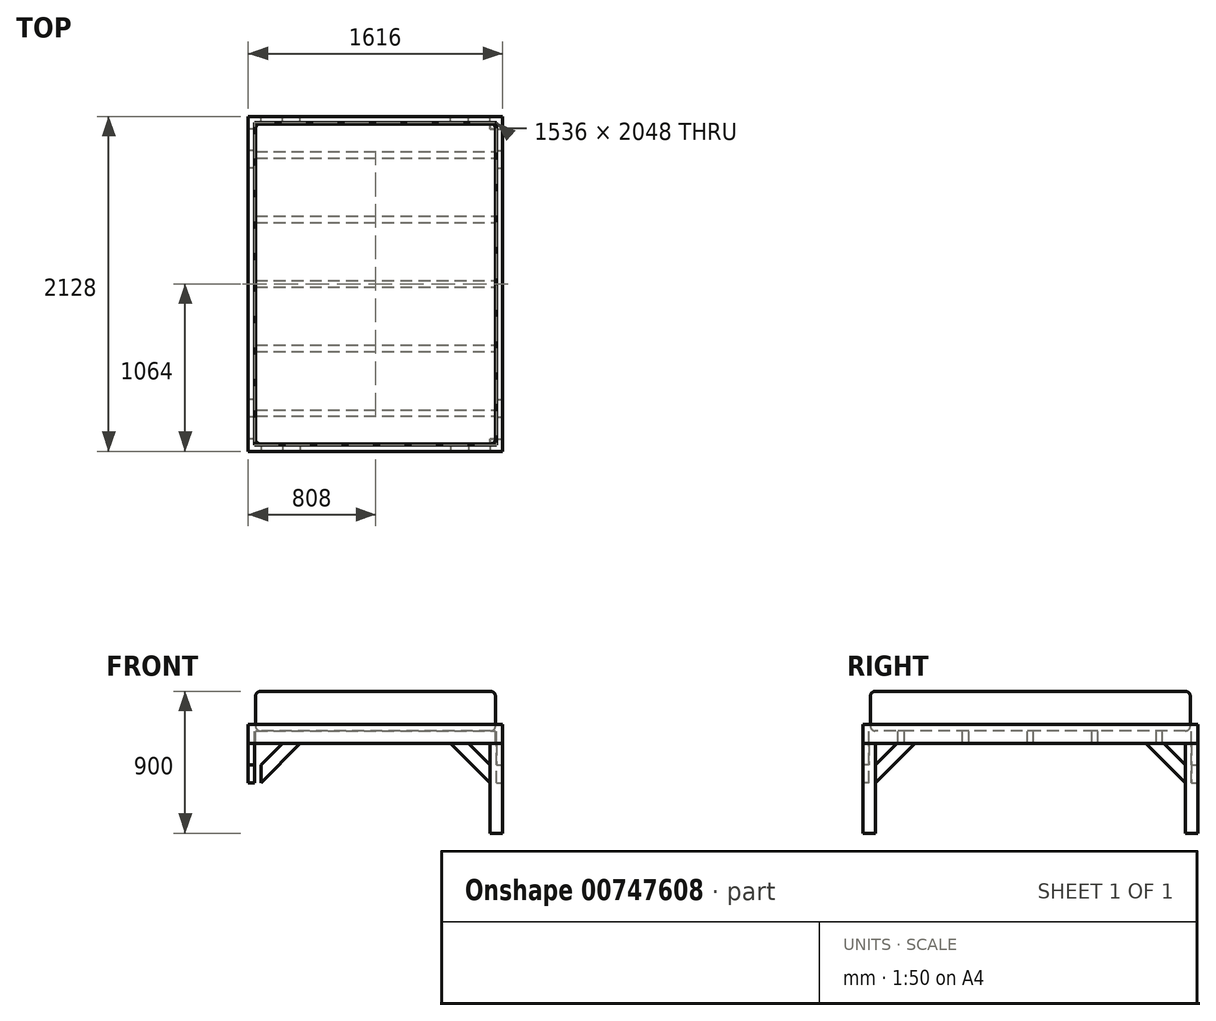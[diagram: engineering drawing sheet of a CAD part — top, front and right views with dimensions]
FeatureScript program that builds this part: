
annotation { "Feature Type Name" : "Feature", "Feature Type Description" : "" }
export const myFeature = defineFeature(function(context is Context, id is Id, definition is map)
    precondition{}
    {
        {
            assignVariable(context, id + "F0", {"name" : "profile", "anyValue" : 40 * mm});
        }
        {
            var Q0;
            Q0=qCreatedBy(makeId("Top.planeOp"),FACE);
            var sketch = newSketch(context, id + "F1", { "sketchPlane" : qUnion([Q0])});
            skLineSegment(sketch, "E0.bottom", {"start": v(762, 1016) * mm, "end": v(-762, 1016) * mm});
            skLineSegment(sketch, "E0.top", {"start": v(762, -1016) * mm, "end": v(-762, -1016) * mm});
            skLineSegment(sketch, "E0.left", {"start": v(762, 1016) * mm, "end": v(762, -1016) * mm});
            skLineSegment(sketch, "E0.right", {"start": v(-762, 1016) * mm, "end": v(-762, -1016) * mm});
            skPoint(sketch, "E0.middle", {"position": v(0, 0) * mm});
            skSolve(sketch);
        }
        {
            var Q0;
            Q0=makeQuery(id+"F1.imprint","IMPRINT",FACE,{"disambiguationData":[TD([[makeQuery(id+"F1.imprint","IMPRINT",EDGE,{"derivedFrom":sQuery(id+"F1.wireOp",EDGE,"E0.bottom")}),1.0]])]});
            extrude(context, id + "F2", {"entities" : qUnion([Q0]), "depth" : 250 * mm, "offsetDistance" : 25 * mm});
        }
        {
            var Q0;
            Q0=makeQuery(id+"F2.opExtrude","CAP_EDGE",EDGE,{"disambiguationData":[OSD([sQuery(id+"F1.wireOp",EDGE,"E0.right")])],"isStart":false});
            var Q1;
            Q1=makeQuery(id+"F2.opExtrude","CAP_EDGE",EDGE,{"disambiguationData":[OSD([sQuery(id+"F1.wireOp",EDGE,"E0.bottom")])],"isStart":false});
            var Q2;
            Q2=makeQuery(id+"F2.opExtrude","CAP_EDGE",EDGE,{"disambiguationData":[OSD([sQuery(id+"F1.wireOp",EDGE,"E0.left")])],"isStart":false});
            var Q3;
            Q3=makeQuery(id+"F2.opExtrude","CAP_EDGE",EDGE,{"disambiguationData":[OSD([sQuery(id+"F1.wireOp",EDGE,"E0.top")])],"isStart":false});
            var Q4;
            Q4=makeQuery(id+"F2.opExtrude","SWEPT_EDGE",EDGE,{"disambiguationData":[OSD([sQuery(id+"F1.wireOp",EDGE,"E0.top"),sQuery(id+"F1.wireOp",EDGE,"E0.right")])]});
            var Q5;
            Q5=makeQuery(id+"F2.opExtrude","SWEPT_EDGE",EDGE,{"disambiguationData":[OSD([sQuery(id+"F1.wireOp",EDGE,"E0.bottom"),sQuery(id+"F1.wireOp",EDGE,"E0.right")])]});
            var Q6;
            Q6=makeQuery(id+"F2.opExtrude","SWEPT_EDGE",EDGE,{"disambiguationData":[OSD([sQuery(id+"F1.wireOp",EDGE,"E0.top"),sQuery(id+"F1.wireOp",EDGE,"E0.left")])]});
            var Q7;
            Q7=makeQuery(id+"F2.opExtrude","CAP_EDGE",EDGE,{"disambiguationData":[OSD([sQuery(id+"F1.wireOp",EDGE,"E0.top")])],"isStart":true});
            var Q8;
            Q8=makeQuery(id+"F2.opExtrude","CAP_EDGE",EDGE,{"disambiguationData":[OSD([sQuery(id+"F1.wireOp",EDGE,"E0.right")])],"isStart":true});
            var Q9;
            Q9=makeQuery(id+"F2.opExtrude","SWEPT_EDGE",EDGE,{"disambiguationData":[OSD([sQuery(id+"F1.wireOp",EDGE,"E0.bottom"),sQuery(id+"F1.wireOp",EDGE,"E0.left")])]});
            var Q10;
            Q10=makeQuery(id+"F2.opExtrude","CAP_EDGE",EDGE,{"disambiguationData":[OSD([sQuery(id+"F1.wireOp",EDGE,"E0.left")])],"isStart":true});
            var Q11;
            Q11=makeQuery(id+"F2.opExtrude","CAP_EDGE",EDGE,{"disambiguationData":[OSD([sQuery(id+"F1.wireOp",EDGE,"E0.bottom")])],"isStart":true});
            fillet(context, id + "F3", {"entities" : qUnion([Q0, Q1, Q2, Q3, Q4, Q5, Q6, Q7, Q8, Q9, Q10, Q11]), "radius" : 30 * mm, "tangentPropagation" : true, "allowEdgeOverflow" : false});
        }
        {
            var Q0;
            Q0=makeQuery(id+"F1.imprint","IMPRINT",FACE,{"disambiguationData":[TD([[makeQuery(id+"F1.imprint","IMPRINT",EDGE,{"derivedFrom":sQuery(id+"F1.wireOp",EDGE,"E0.bottom")}),1.0]])]});
            var sketch = newSketch(context, id + "F4", { "sketchPlane" : qUnion([Q0])});
            skLineSegment(sketch, "E1.bottom", {"start": v(768, 1024) * mm, "end": v(-768, 1024) * mm});
            skLineSegment(sketch, "E1.top", {"start": v(768, -1024) * mm, "end": v(-768, -1024) * mm});
            skLineSegment(sketch, "E1.left", {"start": v(768, 1024) * mm, "end": v(768, -1024) * mm});
            skLineSegment(sketch, "E1.right", {"start": v(-768, 1024) * mm, "end": v(-768, -1024) * mm});
            skPoint(sketch, "E1.middle", {"position": v(0, 0) * mm});
            skLineSegment(sketch, "E2.bottom", {"start": v(808, 1064) * mm, "end": v(-808, 1064) * mm});
            skLineSegment(sketch, "E2.top", {"start": v(808, -1064) * mm, "end": v(-808, -1064) * mm});
            skLineSegment(sketch, "E2.left", {"start": v(808, 1064) * mm, "end": v(808, -1064) * mm});
            skLineSegment(sketch, "E2.right", {"start": v(-808, 1064) * mm, "end": v(-808, -1064) * mm});
            skLineSegment(sketch, "E3", {"start": v(-768, 1024) * mm, "end": v(-768, 1064) * mm});
            skLineSegment(sketch, "E4", {"start": v(768, 1024) * mm, "end": v(768, 1064) * mm});
            skLineSegment(sketch, "E5", {"start": v(768, -1024) * mm, "end": v(768, -1064) * mm});
            skLineSegment(sketch, "E6", {"start": v(-768, -1024) * mm, "end": v(-768, -1064) * mm});
            skLineSegment(sketch, "E7.bottom", {"start": v(-768, 840) * mm, "end": v(768, 840) * mm});
            skLineSegment(sketch, "E7.top", {"start": v(-768, 800) * mm, "end": v(768, 800) * mm});
            skLineSegment(sketch, "E7.left", {"start": v(-768, 840) * mm, "end": v(-768, 800) * mm});
            skLineSegment(sketch, "E7.right", {"start": v(768, 840) * mm, "end": v(768, 800) * mm});
            skLineSegment(sketch, "E8.bottom", {"start": v(-768, 20) * mm, "end": v(768, 20) * mm});
            skLineSegment(sketch, "E8.top", {"start": v(-768, -20) * mm, "end": v(768, -20) * mm});
            skLineSegment(sketch, "E8.left", {"start": v(-768, 20) * mm, "end": v(-768, -20) * mm});
            skLineSegment(sketch, "E8.right", {"start": v(768, 20) * mm, "end": v(768, -20) * mm});
            skLineSegment(sketch, "E9.bottom", {"start": v(-768, -800) * mm, "end": v(768, -800) * mm});
            skLineSegment(sketch, "E9.top", {"start": v(-768, -840) * mm, "end": v(768, -840) * mm});
            skLineSegment(sketch, "E9.left", {"start": v(-768, -800) * mm, "end": v(-768, -840) * mm});
            skLineSegment(sketch, "E9.right", {"start": v(768, -800) * mm, "end": v(768, -840) * mm});
            skLineSegment(sketch, "E10.bottom", {"start": v(-768, 430) * mm, "end": v(768, 430) * mm});
            skLineSegment(sketch, "E10.top", {"start": v(-768, 390) * mm, "end": v(768, 390) * mm});
            skLineSegment(sketch, "E10.left", {"start": v(-768, 430) * mm, "end": v(-768, 390) * mm});
            skLineSegment(sketch, "E10.right", {"start": v(768, 430) * mm, "end": v(768, 390) * mm});
            skLineSegment(sketch, "E11.bottom", {"start": v(-768, -390) * mm, "end": v(768, -390) * mm});
            skLineSegment(sketch, "E11.top", {"start": v(-768, -430) * mm, "end": v(768, -430) * mm});
            skLineSegment(sketch, "E11.left", {"start": v(-768, -390) * mm, "end": v(-768, -430) * mm});
            skLineSegment(sketch, "E11.right", {"start": v(768, -390) * mm, "end": v(768, -430) * mm});
            skLineSegment(sketch, "E12", {"start": v(442.8, 800) * mm, "end": v(442.8, 430) * mm, "construction": true});
            skLineSegment(sketch, "E13", {"start": v(447.42, 390) * mm, "end": v(447.42, 20) * mm, "construction": true});
            skLineSegment(sketch, "E14", {"start": v(422, -20) * mm, "end": v(422, -390) * mm, "construction": true});
            skLineSegment(sketch, "E15", {"start": v(465.9, -430) * mm, "end": v(465.9, -800) * mm, "construction": true});
            skLineSegment(sketch, "E16", {"start": v(442.8, 615) * mm, "end": v(0, 615) * mm, "construction": true});
            skLineSegment(sketch, "E17", {"start": v(0, 615) * mm, "end": v(0, 800) * mm, "construction": true});
            skLineSegment(sketch, "E18", {"start": v(321.78, -840) * mm, "end": v(321.78, -1024) * mm, "construction": true});
            skLineSegment(sketch, "E19", {"start": v(177.4, 840) * mm, "end": v(177.4, 1024) * mm, "construction": true});
            skSolve(sketch);
        }
        {
            var Q0;
            {var subQ0=sQuery(id+"F4.wireOp",EDGE,"E2.right");Q0=makeQuery(id+"F4.imprint","IMPRINT",FACE,{"disambiguationData":[TD([[makeQuery(id+"F4.imprint","IMPRINT",EDGE,{"derivedFrom":subQ0}),1.0]])]});}
            var Q1;
            {var subQ1=sQuery(id+"F4.wireOp",EDGE,"E2.left");Q1=makeQuery(id+"F4.imprint","IMPRINT",FACE,{"disambiguationData":[TD([[makeQuery(id+"F4.imprint","IMPRINT",EDGE,{"derivedFrom":subQ1}),-1.0]])]});}
            extrude(context, id + "F5", {"entities" : qUnion([Q0, Q1]), "oppositeDirection" : true, "depth" : 2 * getVariable(context, 'profile'), "offsetDistance" : 25 * mm});
        }
        {
            var Q0;
            Q0=makeQuery(id+"F4.imprint","IMPRINT",FACE,{"disambiguationData":[TD([[makeQuery(id+"F4.imprint","IMPRINT",EDGE,{"derivedFrom":sQuery(id+"F4.wireOp",EDGE,"E1.bottom")}),-1.0]])]});
            var Q1;
            {var subQ0=sQuery(id+"F4.wireOp",EDGE,"E7.bottom");var subQ1=makeQuery(id+"F1.imprint","IMPRINT",EDGE,{"derivedFrom":sQuery(id+"F1.wireOp",EDGE,"E0.right")});var subQ2=makeQuery(id+"F4.imprint","INTERSECT",VERTEX,{"derivedFrom":[subQ1,subQ0]});Q1=makeQuery(id+"F4.imprint","IMPRINT",FACE,{"disambiguationData":[TD([[makeQuery(id+"F4.imprint","IMPRINT",EDGE,{"disambiguationData":[TD([[subQ2,-1.0]])],"derivedFrom":subQ0}),-1.0]])]});}
            var Q2;
            {var subQ0=sQuery(id+"F4.wireOp",EDGE,"E10.bottom");var subQ1=makeQuery(id+"F1.imprint","IMPRINT",EDGE,{"derivedFrom":sQuery(id+"F1.wireOp",EDGE,"E0.right")});var subQ2=makeQuery(id+"F4.imprint","INTERSECT",VERTEX,{"derivedFrom":[subQ1,subQ0]});Q2=makeQuery(id+"F4.imprint","IMPRINT",FACE,{"disambiguationData":[TD([[makeQuery(id+"F4.imprint","IMPRINT",EDGE,{"disambiguationData":[TD([[subQ2,-1.0]])],"derivedFrom":subQ0}),-1.0]])]});}
            var Q3;
            {var subQ0=sQuery(id+"F4.wireOp",EDGE,"E8.bottom");var subQ1=makeQuery(id+"F1.imprint","IMPRINT",EDGE,{"derivedFrom":sQuery(id+"F1.wireOp",EDGE,"E0.right")});var subQ2=makeQuery(id+"F4.imprint","INTERSECT",VERTEX,{"derivedFrom":[subQ1,subQ0]});Q3=makeQuery(id+"F4.imprint","IMPRINT",FACE,{"disambiguationData":[TD([[makeQuery(id+"F4.imprint","IMPRINT",EDGE,{"disambiguationData":[TD([[subQ2,-1.0]])],"derivedFrom":subQ0}),-1.0]])]});}
            var Q4;
            {var subQ0=sQuery(id+"F4.wireOp",EDGE,"E11.bottom");var subQ1=makeQuery(id+"F1.imprint","IMPRINT",EDGE,{"derivedFrom":sQuery(id+"F1.wireOp",EDGE,"E0.right")});var subQ2=makeQuery(id+"F4.imprint","INTERSECT",VERTEX,{"derivedFrom":[subQ1,subQ0]});Q4=makeQuery(id+"F4.imprint","IMPRINT",FACE,{"disambiguationData":[TD([[makeQuery(id+"F4.imprint","IMPRINT",EDGE,{"disambiguationData":[TD([[subQ2,-1.0]])],"derivedFrom":subQ0}),-1.0]])]});}
            var Q5;
            {var subQ0=sQuery(id+"F4.wireOp",EDGE,"E9.bottom");var subQ1=makeQuery(id+"F1.imprint","IMPRINT",EDGE,{"derivedFrom":sQuery(id+"F1.wireOp",EDGE,"E0.right")});var subQ2=makeQuery(id+"F4.imprint","INTERSECT",VERTEX,{"derivedFrom":[subQ1,subQ0]});Q5=makeQuery(id+"F4.imprint","IMPRINT",FACE,{"disambiguationData":[TD([[makeQuery(id+"F4.imprint","IMPRINT",EDGE,{"disambiguationData":[TD([[subQ2,-1.0]])],"derivedFrom":subQ0}),-1.0]])]});}
            var Q6;
            Q6=makeQuery(id+"F4.imprint","IMPRINT",FACE,{"disambiguationData":[TD([[makeQuery(id+"F4.imprint","IMPRINT",EDGE,{"derivedFrom":sQuery(id+"F4.wireOp",EDGE,"E1.top")}),1.0]])]});
            extrude(context, id + "F6", {"entities" : qUnion([Q0, Q1, Q2, Q3, Q4, Q5, Q6]), "oppositeDirection" : true, "depth" : 2 * getVariable(context, 'profile'), "offsetDistance" : 25 * mm});
        }
        {
            var Q0;
            {var subQ1=sQuery(id+"F4.wireOp",EDGE,"E2.left");Q0=makeQuery(id+"F4.imprint","IMPRINT",FACE,{"disambiguationData":[TD([[makeQuery(id+"F4.imprint","IMPRINT",EDGE,{"derivedFrom":subQ1}),-1.0]])]});}
            extrude(context, id + "F7", {"entities" : qUnion([Q0]), "operationType" : NewBodyOperationType.ADD, "depth" : getVariable(context, 'profile'), "offsetDistance" : 25 * mm});
        }
        {
            var Q0;
            Q0=makeQuery(id+"F4.imprint","IMPRINT",FACE,{"disambiguationData":[TD([[makeQuery(id+"F4.imprint","IMPRINT",EDGE,{"derivedFrom":sQuery(id+"F4.wireOp",EDGE,"E1.bottom")}),-1.0]])]});
            extrude(context, id + "F8", {"entities" : qUnion([Q0]), "operationType" : NewBodyOperationType.ADD, "depth" : getVariable(context, 'profile'), "offsetDistance" : 25 * mm});
        }
        {
            var Q0;
            {var subQ0=sQuery(id+"F4.wireOp",EDGE,"E2.right");Q0=makeQuery(id+"F4.imprint","IMPRINT",FACE,{"disambiguationData":[TD([[makeQuery(id+"F4.imprint","IMPRINT",EDGE,{"derivedFrom":subQ0}),1.0]])]});}
            extrude(context, id + "F9", {"entities" : qUnion([Q0]), "operationType" : NewBodyOperationType.ADD, "depth" : getVariable(context, 'profile'), "offsetDistance" : 25 * mm});
        }
        {
            var Q0;
            Q0=makeQuery(id+"F4.imprint","IMPRINT",FACE,{"disambiguationData":[TD([[makeQuery(id+"F4.imprint","IMPRINT",EDGE,{"derivedFrom":sQuery(id+"F4.wireOp",EDGE,"E1.top")}),1.0]])]});
            extrude(context, id + "F10", {"entities" : qUnion([Q0]), "operationType" : NewBodyOperationType.ADD, "depth" : getVariable(context, 'profile'), "offsetDistance" : 25 * mm});
        }
        {
            var Q0;
            Q0=makeQuery(id+"F5.opExtrude","CAP_FACE",FACE,{"disambiguationData":[OSD([sQuery(id+"F4.wireOp",EDGE,"E1.left"),sQuery(id+"F4.wireOp",EDGE,"E2.bottom"),sQuery(id+"F4.wireOp",EDGE,"E2.top"),sQuery(id+"F4.wireOp",EDGE,"E2.left"),sQuery(id+"F4.wireOp",EDGE,"E4"),sQuery(id+"F4.wireOp",EDGE,"E5"),sQuery(id+"F4.wireOp",EDGE,"E7.right"),sQuery(id+"F4.wireOp",EDGE,"E8.right"),sQuery(id+"F4.wireOp",EDGE,"E9.right"),sQuery(id+"F4.wireOp",EDGE,"E10.right"),sQuery(id+"F4.wireOp",EDGE,"E11.right")])],"isStart":false});
            var sketch = newSketch(context, id + "F11", { "sketchPlane" : qUnion([Q0])});
            skPoint(sketch, "E20.0", {"position": v(808, 1064) * mm});
            skPoint(sketch, "E21.0", {"position": v(808, -1064) * mm});
            skPoint(sketch, "E22.0", {"position": v(-808, -1064) * mm});
            skPoint(sketch, "E23.0", {"position": v(-808, 1064) * mm});
            skLineSegment(sketch, "E24.bottom", {"start": v(-808, 1064) * mm, "end": v(-728, 1064) * mm});
            skLineSegment(sketch, "E24.top", {"start": v(-808, 984) * mm, "end": v(-728, 984) * mm});
            skLineSegment(sketch, "E24.left", {"start": v(-808, 1064) * mm, "end": v(-808, 984) * mm});
            skLineSegment(sketch, "E24.right", {"start": v(-728, 1064) * mm, "end": v(-728, 984) * mm});
            skLineSegment(sketch, "E25.bottom", {"start": v(808, 1064) * mm, "end": v(728, 1064) * mm});
            skLineSegment(sketch, "E25.top", {"start": v(808, 984) * mm, "end": v(728, 984) * mm});
            skLineSegment(sketch, "E25.left", {"start": v(808, 1064) * mm, "end": v(808, 984) * mm});
            skLineSegment(sketch, "E25.right", {"start": v(728, 1064) * mm, "end": v(728, 984) * mm});
            skLineSegment(sketch, "E26.bottom", {"start": v(808, -1064) * mm, "end": v(728, -1064) * mm});
            skLineSegment(sketch, "E26.top", {"start": v(808, -984) * mm, "end": v(728, -984) * mm});
            skLineSegment(sketch, "E26.left", {"start": v(808, -1064) * mm, "end": v(808, -984) * mm});
            skLineSegment(sketch, "E26.right", {"start": v(728, -1064) * mm, "end": v(728, -984) * mm});
            skLineSegment(sketch, "E27.bottom", {"start": v(-808, -1064) * mm, "end": v(-728, -1064) * mm});
            skLineSegment(sketch, "E27.top", {"start": v(-808, -984) * mm, "end": v(-728, -984) * mm});
            skLineSegment(sketch, "E27.left", {"start": v(-808, -1064) * mm, "end": v(-808, -984) * mm});
            skLineSegment(sketch, "E27.right", {"start": v(-728, -1064) * mm, "end": v(-728, -984) * mm});
            skSolve(sketch);
        }
        {
            var Q0;
            Q0=makeQuery(id+"F2.opExtrude","CAP_FACE",FACE,{"disambiguationData":[OSD([sQuery(id+"F1.wireOp",EDGE,"E0.bottom"),sQuery(id+"F1.wireOp",EDGE,"E0.top"),sQuery(id+"F1.wireOp",EDGE,"E0.left"),sQuery(id+"F1.wireOp",EDGE,"E0.right")])],"isStart":false});
            cPlane(context, id + "F12", {"entities" : qUnion([Q0]), "cplaneType" : CPlaneType.OFFSET, "offset" : 900 * mm, "oppositeDirection" : true, "width" : 150 * mm, "height" : 150 * mm});
        }
        {
            var Q0;
            Q0=makeQuery(id+"F11.imprint","IMPRINT",FACE,{"disambiguationData":[TD([[makeQuery(id+"F11.imprint","IMPRINT",EDGE,{"derivedFrom":sQuery(id+"F11.wireOp",EDGE,"E24.bottom")}),-1.0]])]});
            var Q1;
            {var subQ0=sQuery(id+"F11.wireOp",EDGE,"E25.left");Q1=makeQuery(id+"F11.imprint","IMPRINT",FACE,{"disambiguationData":[TD([[makeQuery(id+"F11.imprint","IMPRINT",EDGE,{"derivedFrom":subQ0}),1.0]])]});}
            var Q2;
            {var subQ3=sQuery(id+"F11.wireOp",EDGE,"E25.right");Q2=makeQuery(id+"F11.imprint","IMPRINT",FACE,{"disambiguationData":[TD([[makeQuery(id+"F11.imprint","IMPRINT",EDGE,{"derivedFrom":subQ3}),1.0]])]});}
            var Q3;
            {var subQ0=sQuery(id+"F11.wireOp",EDGE,"E26.left");Q3=makeQuery(id+"F11.imprint","IMPRINT",FACE,{"disambiguationData":[TD([[makeQuery(id+"F11.imprint","IMPRINT",EDGE,{"derivedFrom":subQ0}),1.0]])]});}
            var Q4;
            {var subQ3=sQuery(id+"F11.wireOp",EDGE,"E26.right");Q4=makeQuery(id+"F11.imprint","IMPRINT",FACE,{"disambiguationData":[TD([[makeQuery(id+"F11.imprint","IMPRINT",EDGE,{"derivedFrom":subQ3}),-1.0]])]});}
            var Q5;
            Q5=makeQuery(id+"F11.imprint","IMPRINT",FACE,{"disambiguationData":[TD([[makeQuery(id+"F11.imprint","IMPRINT",EDGE,{"derivedFrom":sQuery(id+"F11.wireOp",EDGE,"E27.bottom")}),1.0]])]});
            var Q6;
            Q6=qCreatedBy(id+"F12.planeOp",FACE);
            extrude(context, id + "F13", {"entities" : qUnion([Q0, Q1, Q2, Q3, Q4, Q5]), "endBound" : BoundingType.UP_TO_SURFACE, "depth" : 25 * mm, "endBoundEntityFace" : qUnion([Q6]), "offsetDistance" : 25 * mm});
        }
        {
            var Q0;
            {var subQ0=sQuery(id+"F4.wireOp",EDGE,"E2.top");Q0=makeQuery(id+"F10.boolean.opBoolean","MERGE",FACE,{"derivedFrom":[makeQuery(id+"F6.opExtrude","SWEPT_FACE",FACE,{"disambiguationData":[OSD([subQ0])]}),makeQuery(id+"F10.opExtrude","SWEPT_FACE",FACE,{"disambiguationData":[OSD([subQ0])]})]});}
            var sketch = newSketch(context, id + "F14", { "sketchPlane" : qUnion([Q0])});
            skLineSegment(sketch, "E28.0", {"start": v(-728, -650) * mm, "end": v(-728, -80) * mm});
            skLineSegment(sketch, "E29", {"start": v(-591.14, -80) * mm, "end": v(-728, -216.86) * mm});
            skLineSegment(sketch, "E30", {"start": v(-728, -330) * mm, "end": v(-478, -80) * mm});
            skLineSegment(sketch, "E31.0", {"start": v(728, -650) * mm, "end": v(728, -80) * mm});
            skLineSegment(sketch, "E32", {"start": v(591.14, -80) * mm, "end": v(728, -216.86) * mm});
            skLineSegment(sketch, "E33", {"start": v(728, -330) * mm, "end": v(478, -80) * mm});
            skSolve(sketch);
        }
        {
            var Q0;
            {var subQ0=sQuery(id+"F14.wireOp",EDGE,"E29");Q0=makeQuery(id+"F14.imprint","IMPRINT",FACE,{"disambiguationData":[TD([[makeQuery(id+"F14.imprint","IMPRINT",EDGE,{"derivedFrom":subQ0}),1.0]])]});}
            var Q1;
            {var subQ0=sQuery(id+"F14.wireOp",EDGE,"E32");Q1=makeQuery(id+"F14.imprint","IMPRINT",FACE,{"disambiguationData":[TD([[makeQuery(id+"F14.imprint","IMPRINT",EDGE,{"derivedFrom":subQ0}),-1.0]])]});}
            var Q2;
            {var subQ0=sQuery(id+"F4.wireOp",EDGE,"E1.top");Q2=makeQuery(id+"F10.boolean.opBoolean","MERGE",FACE,{"derivedFrom":[makeQuery(id+"F6.opExtrude","SWEPT_FACE",FACE,{"disambiguationData":[OSD([subQ0])]}),makeQuery(id+"F10.opExtrude","SWEPT_FACE",FACE,{"disambiguationData":[OSD([subQ0])]})]});}
            extrude(context, id + "F15", {"entities" : qUnion([Q0, Q1]), "endBound" : BoundingType.UP_TO_SURFACE, "oppositeDirection" : true, "depth" : 25 * mm, "endBoundEntityFace" : qUnion([Q2]), "offsetDistance" : 25 * mm});
        }
        {
            var Q0;
            {var subQ0=sQuery(id+"F4.wireOp",EDGE,"E2.bottom");Q0=makeQuery(id+"F8.boolean.opBoolean","MERGE",FACE,{"derivedFrom":[makeQuery(id+"F6.opExtrude","SWEPT_FACE",FACE,{"disambiguationData":[OSD([subQ0])]}),makeQuery(id+"F8.opExtrude","SWEPT_FACE",FACE,{"disambiguationData":[OSD([subQ0])]})]});}
            var sketch = newSketch(context, id + "F16", { "sketchPlane" : qUnion([Q0])});
            skLineSegment(sketch, "E34.0.0", {"start": v(-728, -216.86) * mm, "end": v(-728, -330) * mm});
            skLineSegment(sketch, "E34.0.1", {"start": v(-728, -330) * mm, "end": v(-478, -80) * mm});
            skLineSegment(sketch, "E34.0.2", {"start": v(-478, -80) * mm, "end": v(-591.14, -80) * mm});
            skLineSegment(sketch, "E34.0.3", {"start": v(-591.14, -80) * mm, "end": v(-728, -216.86) * mm});
            skLineSegment(sketch, "E35.0.0", {"start": v(478, -80) * mm, "end": v(728, -330) * mm});
            skLineSegment(sketch, "E35.0.1", {"start": v(728, -330) * mm, "end": v(728, -216.86) * mm});
            skLineSegment(sketch, "E35.0.2", {"start": v(728, -216.86) * mm, "end": v(591.14, -80) * mm});
            skLineSegment(sketch, "E35.0.3", {"start": v(591.14, -80) * mm, "end": v(478, -80) * mm});
            skSolve(sketch);
        }
        {
            var Q0;
            Q0 = qSketchRegion(id + "F16", true);
            var Q1;
            {var subQ0=sQuery(id+"F4.wireOp",EDGE,"E1.bottom");Q1=makeQuery(id+"F8.boolean.opBoolean","MERGE",FACE,{"derivedFrom":[makeQuery(id+"F6.opExtrude","SWEPT_FACE",FACE,{"disambiguationData":[OSD([subQ0])]}),makeQuery(id+"F8.opExtrude","SWEPT_FACE",FACE,{"disambiguationData":[OSD([subQ0])]})]});}
            extrude(context, id + "F17", {"entities" : qUnion([Q0]), "endBound" : BoundingType.UP_TO_SURFACE, "oppositeDirection" : true, "depth" : 25 * mm, "endBoundEntityFace" : qUnion([Q1]), "offsetDistance" : 25 * mm});
        }
        {
            var Q0;
            {var subQ0=sQuery(id+"F4.wireOp",EDGE,"E2.left");Q0=makeQuery(id+"F7.boolean.opBoolean","MERGE",FACE,{"derivedFrom":[makeQuery(id+"F5.opExtrude","SWEPT_FACE",FACE,{"disambiguationData":[OSD([subQ0])]}),makeQuery(id+"F7.opExtrude","SWEPT_FACE",FACE,{"disambiguationData":[OSD([subQ0])]})]});}
            var sketch = newSketch(context, id + "F18", { "sketchPlane" : qUnion([Q0])});
            skPoint(sketch, "E36.0", {"position": v(1064, -330) * mm});
            skLineSegment(sketch, "E37.0", {"start": v(984, -650) * mm, "end": v(984, -80) * mm});
            skLineSegment(sketch, "E38.0", {"start": v(-984, -650) * mm, "end": v(-984, -80) * mm});
            skLineSegment(sketch, "E39", {"start": v(847.14, -80) * mm, "end": v(984, -216.86) * mm});
            skLineSegment(sketch, "E40", {"start": v(984, -330) * mm, "end": v(734, -80) * mm});
            skLineSegment(sketch, "E41", {"start": v(-984, -216.86) * mm, "end": v(-847.14, -80) * mm});
            skLineSegment(sketch, "E42", {"start": v(-734, -80) * mm, "end": v(-984, -330) * mm});
            skSolve(sketch);
        }
        {
            var Q0;
            {var subQ0=sQuery(id+"F18.wireOp",EDGE,"E41");Q0=makeQuery(id+"F18.imprint","IMPRINT",FACE,{"disambiguationData":[TD([[makeQuery(id+"F18.imprint","IMPRINT",EDGE,{"derivedFrom":subQ0}),-1.0]])]});}
            var Q1;
            {var subQ0=sQuery(id+"F18.wireOp",EDGE,"E39");Q1=makeQuery(id+"F18.imprint","IMPRINT",FACE,{"disambiguationData":[TD([[makeQuery(id+"F18.imprint","IMPRINT",EDGE,{"derivedFrom":subQ0}),-1.0]])]});}
            var Q2;
            {var subQ0=sQuery(id+"F4.wireOp",EDGE,"E11.right");var subQ1=sQuery(id+"F4.wireOp",EDGE,"E10.right");var subQ2=sQuery(id+"F4.wireOp",EDGE,"E9.right");var subQ3=sQuery(id+"F4.wireOp",EDGE,"E8.right");var subQ4=sQuery(id+"F4.wireOp",EDGE,"E7.right");var subQ5=sQuery(id+"F4.wireOp",EDGE,"E5");var subQ6=sQuery(id+"F4.wireOp",EDGE,"E4");var subQ7=sQuery(id+"F4.wireOp",EDGE,"E1.left");Q2=makeQuery(id+"F7.boolean.opBoolean","MERGE",FACE,{"derivedFrom":[makeQuery(id+"F5.opExtrude","SWEPT_FACE",FACE,{"disambiguationData":[OSD([subQ7,subQ6,subQ5,subQ4,subQ3,subQ2,subQ1,subQ0])]}),makeQuery(id+"F7.opExtrude","SWEPT_FACE",FACE,{"disambiguationData":[OSD([subQ7,subQ6,subQ5,subQ4,subQ3,subQ2,subQ1,subQ0])]})]});}
            extrude(context, id + "F19", {"entities" : qUnion([Q0, Q1]), "endBound" : BoundingType.UP_TO_SURFACE, "oppositeDirection" : true, "depth" : 25 * mm, "endBoundEntityFace" : qUnion([Q2]), "offsetDistance" : 25 * mm});
        }
        {
            var Q0;
            {var subQ0=sQuery(id+"F4.wireOp",EDGE,"E2.right");Q0=makeQuery(id+"F9.boolean.opBoolean","MERGE",FACE,{"derivedFrom":[makeQuery(id+"F5.opExtrude","SWEPT_FACE",FACE,{"disambiguationData":[OSD([subQ0])]}),makeQuery(id+"F9.opExtrude","SWEPT_FACE",FACE,{"disambiguationData":[OSD([subQ0])]})]});}
            var sketch = newSketch(context, id + "F20", { "sketchPlane" : qUnion([Q0])});
            skLineSegment(sketch, "E43.0.0", {"start": v(-984, -216.86) * mm, "end": v(-984, -330) * mm});
            skLineSegment(sketch, "E43.0.1", {"start": v(-984, -330) * mm, "end": v(-734, -80) * mm});
            skLineSegment(sketch, "E43.0.2", {"start": v(-734, -80) * mm, "end": v(-847.14, -80) * mm});
            skLineSegment(sketch, "E43.0.3", {"start": v(-847.14, -80) * mm, "end": v(-984, -216.86) * mm});
            skLineSegment(sketch, "E44.0.0", {"start": v(847.14, -80) * mm, "end": v(734, -80) * mm});
            skLineSegment(sketch, "E44.0.1", {"start": v(734, -80) * mm, "end": v(984, -330) * mm});
            skLineSegment(sketch, "E44.0.2", {"start": v(984, -330) * mm, "end": v(984, -216.86) * mm});
            skLineSegment(sketch, "E44.0.3", {"start": v(984, -216.86) * mm, "end": v(847.14, -80) * mm});
            skSolve(sketch);
        }
        {
            var Q0;
            Q0 = qSketchRegion(id + "F20", true);
            var Q1;
            {var subQ0=sQuery(id+"F4.wireOp",EDGE,"E11.left");var subQ1=sQuery(id+"F4.wireOp",EDGE,"E10.left");var subQ2=sQuery(id+"F4.wireOp",EDGE,"E9.left");var subQ3=sQuery(id+"F4.wireOp",EDGE,"E8.left");var subQ4=sQuery(id+"F4.wireOp",EDGE,"E7.left");var subQ5=sQuery(id+"F4.wireOp",EDGE,"E6");var subQ6=sQuery(id+"F4.wireOp",EDGE,"E3");var subQ7=sQuery(id+"F4.wireOp",EDGE,"E1.right");Q1=makeQuery(id+"F9.boolean.opBoolean","MERGE",FACE,{"derivedFrom":[makeQuery(id+"F5.opExtrude","SWEPT_FACE",FACE,{"disambiguationData":[OSD([subQ7,subQ6,subQ5,subQ4,subQ3,subQ2,subQ1,subQ0])]}),makeQuery(id+"F9.opExtrude","SWEPT_FACE",FACE,{"disambiguationData":[OSD([subQ7,subQ6,subQ5,subQ4,subQ3,subQ2,subQ1,subQ0])]})]});}
            extrude(context, id + "F21", {"entities" : qUnion([Q0]), "endBound" : BoundingType.UP_TO_SURFACE, "oppositeDirection" : true, "depth" : 25 * mm, "endBoundEntityFace" : qUnion([Q1]), "offsetDistance" : 25 * mm});
        }
    });
